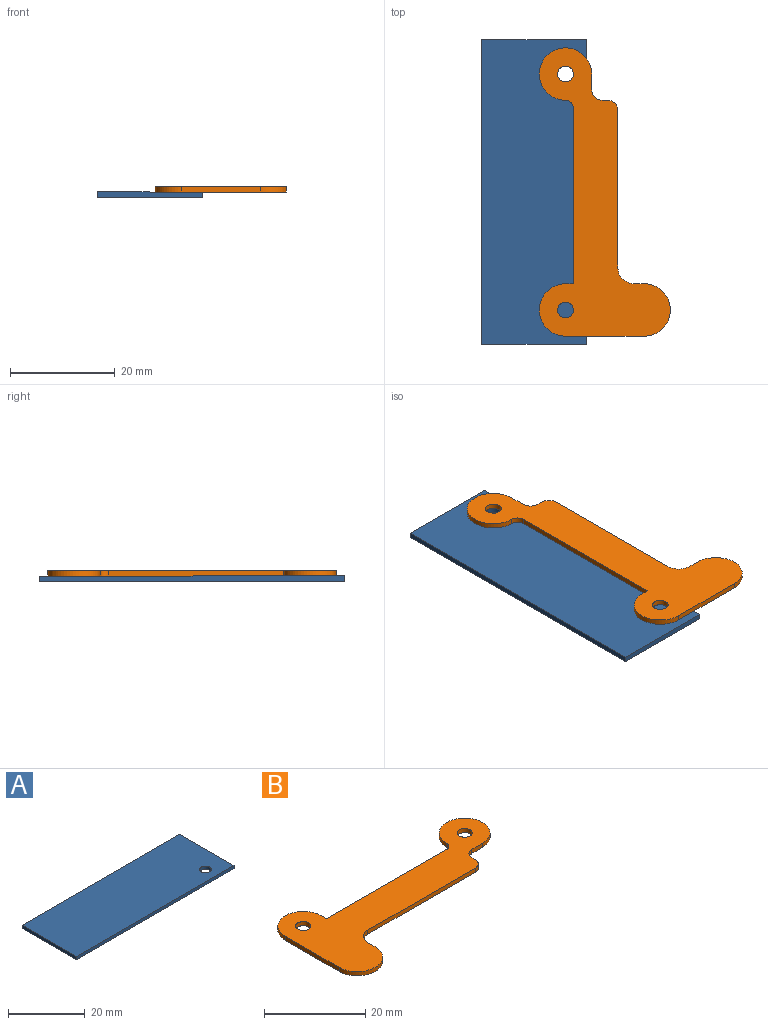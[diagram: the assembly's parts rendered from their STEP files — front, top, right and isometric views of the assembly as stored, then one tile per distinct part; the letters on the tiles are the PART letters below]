
ASSEMBLY  parts=2 mates=1
PART A: 7 faces, bbox 58x20x1 mm
  f0: plane 20x1mm, normal (-1,0,0), area 20mm2, adj f1,f4,f5,f6
  f1: plane 58x1mm, normal (0,-1,0), area 58mm2, adj f0,f2,f5,f6
  f2: plane 20x1mm, normal (1,0,0), area 20mm2, adj f1,f4,f5,f6
  f3: cylinder r=1.5mm len=3mm, axis (0,0,1), area 9.4mm2, adj f5,f6
  f4: plane 58x1mm, normal (0,1,0), area 58mm2, adj f0,f2,f5,f6
  f5: plane 58x20mm, normal (0,0,-1), area 1152.9mm2, adj f0,f1,f2,f3,f4
  f6: plane 58x20mm, normal (0,0,1), area 1152.9mm2, adj f0,f1,f2,f3,f4
PART B: 18 faces, bbox 55x25x1 mm
  f0: plane 15x1mm, normal (-1,0,0), area 15mm2, adj f1,f15,f16,f17
  f1: cylinder r=5mm len=10mm, axis (0,0,-1), area 15.7mm2, adj f0,f2,f16,f17
  f2: plane 2x1mm, normal (1,0,0), area 2mm2, adj f1,f3,f16,f17
  f3: cylinder r=3mm len=3mm, axis (0,0,-1), area 4.7mm2, adj f2,f4,f16,f17
  f4: plane 30x1mm, normal (0,-1,0), area 30mm2, adj f3,f5,f16,f17
  f5: cylinder r=2mm len=2mm, axis (0,0,-1), area 3.1mm2, adj f4,f6,f16,f17
  f6: plane 1x1mm, normal (1,0,0), area 1mm2, adj f5,f7,f16,f17
  f7: cylinder r=2mm len=2mm, axis (0,0,-1), area 3.1mm2, adj f6,f8,f16,f17
  f8: plane 3x1mm, normal (0,-1,0), area 3mm2, adj f7,f9,f16,f17
  f9: cylinder r=5mm len=10mm, axis (0,0,-1), area 23.6mm2, adj f8,f10,f16,f17
  f10: cylinder r=1.5mm len=1.5mm, axis (0,0,-1), area 2.4mm2, adj f9,f11,f16,f17
  f11: plane 33.5x1mm, normal (0,1,0), area 33.5mm2, adj f10,f12,f16,f17
  f12: plane 1.5x1mm, normal (1,0,0), area 1.5mm2, adj f11,f15,f16,f17
  f13: cylinder r=1.5mm len=3mm, axis (0,0,-1), area 9.4mm2, adj f16,f17
  f14: cylinder r=1.5mm len=3mm, axis (0,0,-1), area 9.4mm2, adj f16,f17
  f15: cylinder r=5mm len=10mm, axis (0,0,-1), area 15.7mm2, adj f0,f12,f16,f17
  f16: plane 55x25mm, normal (0,0,1), area 598.2mm2, adj f0,f1,f2,f3,f4,f5,f6,f7
  f17: plane 55x25mm, normal (0,0,-1), area 598.2mm2, adj f0,f1,f2,f3,f4,f5,f6,f7
PLACE A rot(axis=(0,0,1),90deg) t=(42.77,-33.72,2.65)mm
PLACE B rot(axis=(0,0,1),90deg) t=(42.77,-33.72,2.65)mm
MATE revolute A.f3 <-> B.f9  axis (0,0,1) through (32.77,16.28,2.65)mm
